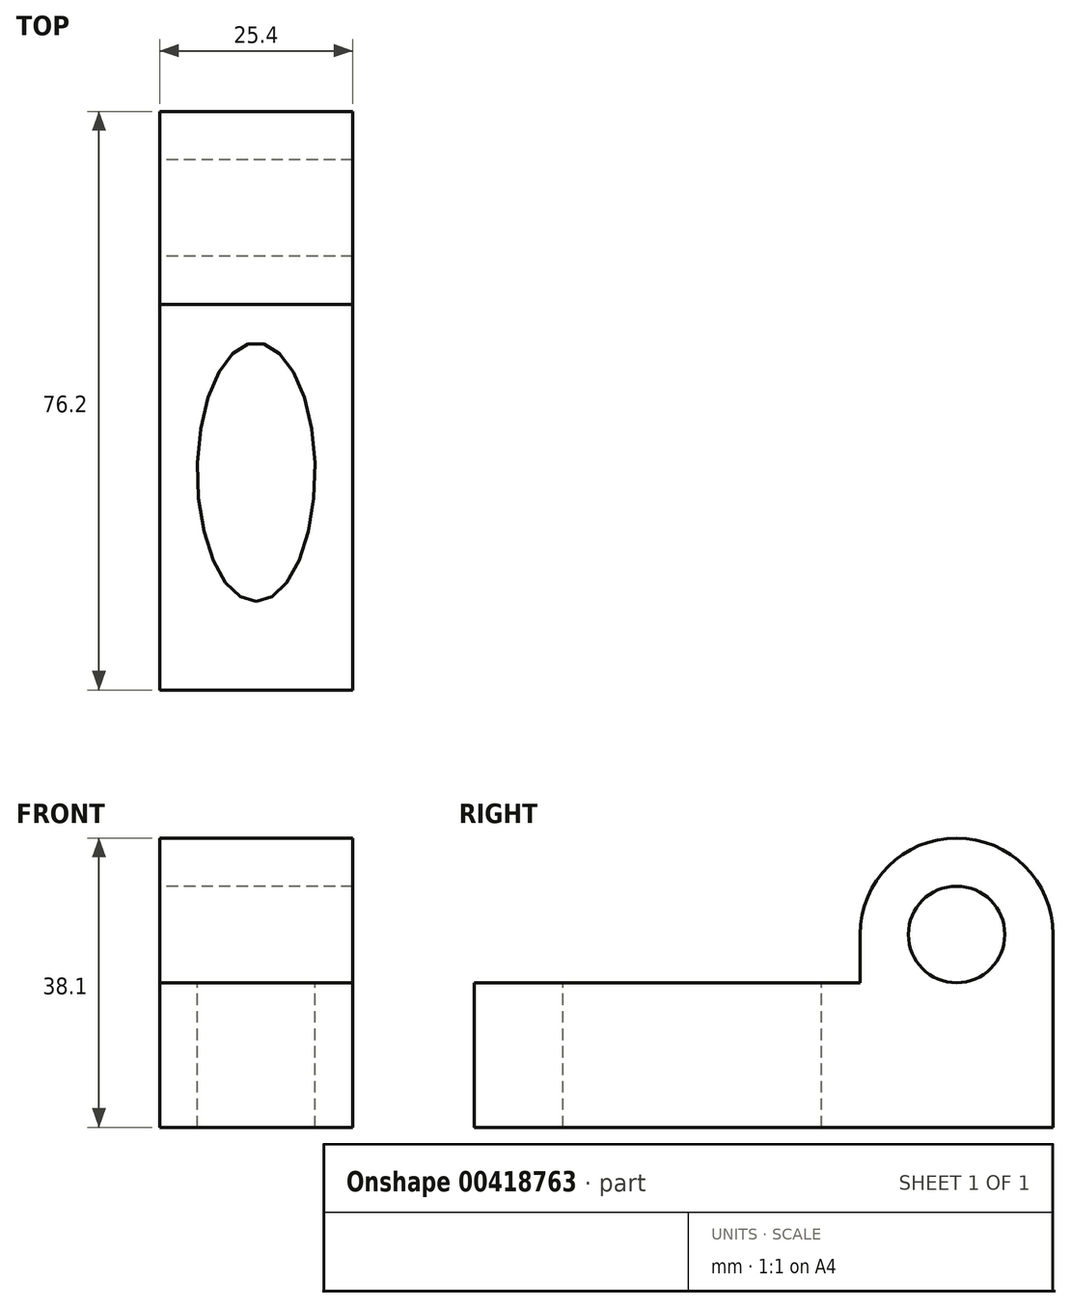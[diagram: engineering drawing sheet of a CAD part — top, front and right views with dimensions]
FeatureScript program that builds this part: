
annotation { "Feature Type Name" : "Feature", "Feature Type Description" : "" }
export const myFeature = defineFeature(function(context is Context, id is Id, definition is map)
    precondition{}
    {
        {
            var Q0;
            Q0=qCreatedBy(makeId("Right.planeOp"),FACE);
            var sketch = newSketch(context, id + "F0", { "sketchPlane" : qUnion([Q0])});
            skLineSegment(sketch, "E0", {"start": v(0, 0) * mm, "end": v(-76.2, 0) * mm});
            skLineSegment(sketch, "E1", {"start": v(-76.2, 0) * mm, "end": v(-76.2, 19.05) * mm});
            skLineSegment(sketch, "E2", {"start": v(-76.2, 19.05) * mm, "end": v(-25.4, 19.05) * mm});
            skLineSegment(sketch, "E3", {"start": v(-25.4, 19.05) * mm, "end": v(-25.4, 38.1) * mm});
            skLineSegment(sketch, "E4", {"start": v(-25.4, 38.1) * mm, "end": v(0, 38.1) * mm});
            skLineSegment(sketch, "E5", {"start": v(0, 38.1) * mm, "end": v(0, 0) * mm});
            skSolve(sketch);
        }
        {
            var Q0;
            Q0 = qSketchRegion(id + "F0", true);
            extrude(context, id + "F1", {"entities" : qUnion([Q0]), "depth" : 25.4 * mm});
        }
        {
            var Q0;
            Q0=makeQuery(id+"F1.opExtrude","CAP_FACE",FACE,{"disambiguationData":[OSD([sQuery(id+"F0.wireOp",EDGE,"E0"),sQuery(id+"F0.wireOp",EDGE,"E1"),sQuery(id+"F0.wireOp",EDGE,"E2"),sQuery(id+"F0.wireOp",EDGE,"E3"),sQuery(id+"F0.wireOp",EDGE,"E4"),sQuery(id+"F0.wireOp",EDGE,"E5")])],"isStart":true});
            var sketch = newSketch(context, id + "F2", { "sketchPlane" : qUnion([Q0])});
            skArc(sketch, "E6", {"start": v(25.4, 25.4) * mm, "mid": v(12.7, 38.1) * mm, "end": v(0, 25.4) * mm});
            skCircle(sketch, "E7", {"center": v(12.7, 25.4) * mm, "radius": 6.35 * mm});
            skSolve(sketch);
        }
        {
            var Q0;
            Q0 = qSketchRegion(id + "F2", true);
            var Q1;
            {var subQ0=sQuery(id+"F2.wireOp",EDGE,"E6");var subQ1=makeQuery(id+"F1.opExtrude","CAP_EDGE",EDGE,{"disambiguationData":[OSD([sQuery(id+"F0.wireOp",EDGE,"E5")])],"isStart":true});var subQ2=makeQuery(id+"F2.imprint","INTERSECT",VERTEX,{"derivedFrom":[subQ1,subQ0]});Q1=makeQuery(id+"F2.imprint","IMPRINT",FACE,{"disambiguationData":[TD([[makeQuery(id+"F2.imprint","IMPRINT",EDGE,{"disambiguationData":[TD([[subQ2,1.0]])],"derivedFrom":subQ0}),-1.0]])]});}
            var Q2;
            {var subQ0=sQuery(id+"F2.wireOp",EDGE,"E6");var subQ1=makeQuery(id+"F1.opExtrude","CAP_EDGE",EDGE,{"disambiguationData":[OSD([sQuery(id+"F0.wireOp",EDGE,"E3")])],"isStart":true});var subQ2=makeQuery(id+"F2.imprint","INTERSECT",VERTEX,{"derivedFrom":[subQ1,subQ0]});Q2=makeQuery(id+"F2.imprint","IMPRINT",FACE,{"disambiguationData":[TD([[makeQuery(id+"F2.imprint","IMPRINT",EDGE,{"disambiguationData":[TD([[subQ2,-1.0]])],"derivedFrom":subQ0}),-1.0]])]});}
            extrude(context, id + "F3", {"entities" : qUnion([Q0, Q1, Q2]), "operationType" : NewBodyOperationType.REMOVE, "oppositeDirection" : true, "depth" : 25.4 * mm});
        }
        {
            var Q0;
            Q0=makeQuery(id+"F1.opExtrude","SWEPT_FACE",FACE,{"disambiguationData":[OSD([sQuery(id+"F0.wireOp",EDGE,"E2")])]});
            var sketch = newSketch(context, id + "F4", { "sketchPlane" : qUnion([Q0])});
            skSolve(sketch);
        }
        {
            var Q0;
            {var subQ0=sQuery(id+"F0.wireOp",EDGE,"E2");Q0=makeQuery(id+"F4.imprint","IMPRINT",FACE,{"disambiguationData":[TD([[makeQuery(id+"F4.imprint","IMPRINT",EDGE,{"derivedFrom":makeQuery(id+"F1.opExtrude","CAP_EDGE",EDGE,{"disambiguationData":[OSD([subQ0])],"isStart":true})}),-1.0]])]});}
            var sketch = newSketch(context, id + "F5", { "sketchPlane" : qUnion([Q0])});
            skEllipse(sketch, "E8", {"center": v(12.7, -47.51) * mm, "majorRadius": 17.02 * mm, "minorRadius": 7.75 * mm, "majorAxis": v(0, -1)});
            skSolve(sketch);
        }
        {
            var Q0;
            Q0=makeQuery(id+"F5.imprint","IMPRINT",FACE,{"disambiguationData":[TD([[makeQuery(id+"F5.imprint","IMPRINT",EDGE,{"derivedFrom":sQuery(id+"F5.wireOp",EDGE,"E8")}),1.0]])]});
            extrude(context, id + "F6", {"entities" : qUnion([Q0]), "operationType" : NewBodyOperationType.REMOVE, "oppositeDirection" : true, "depth" : 25.4 * mm});
        }
    });
